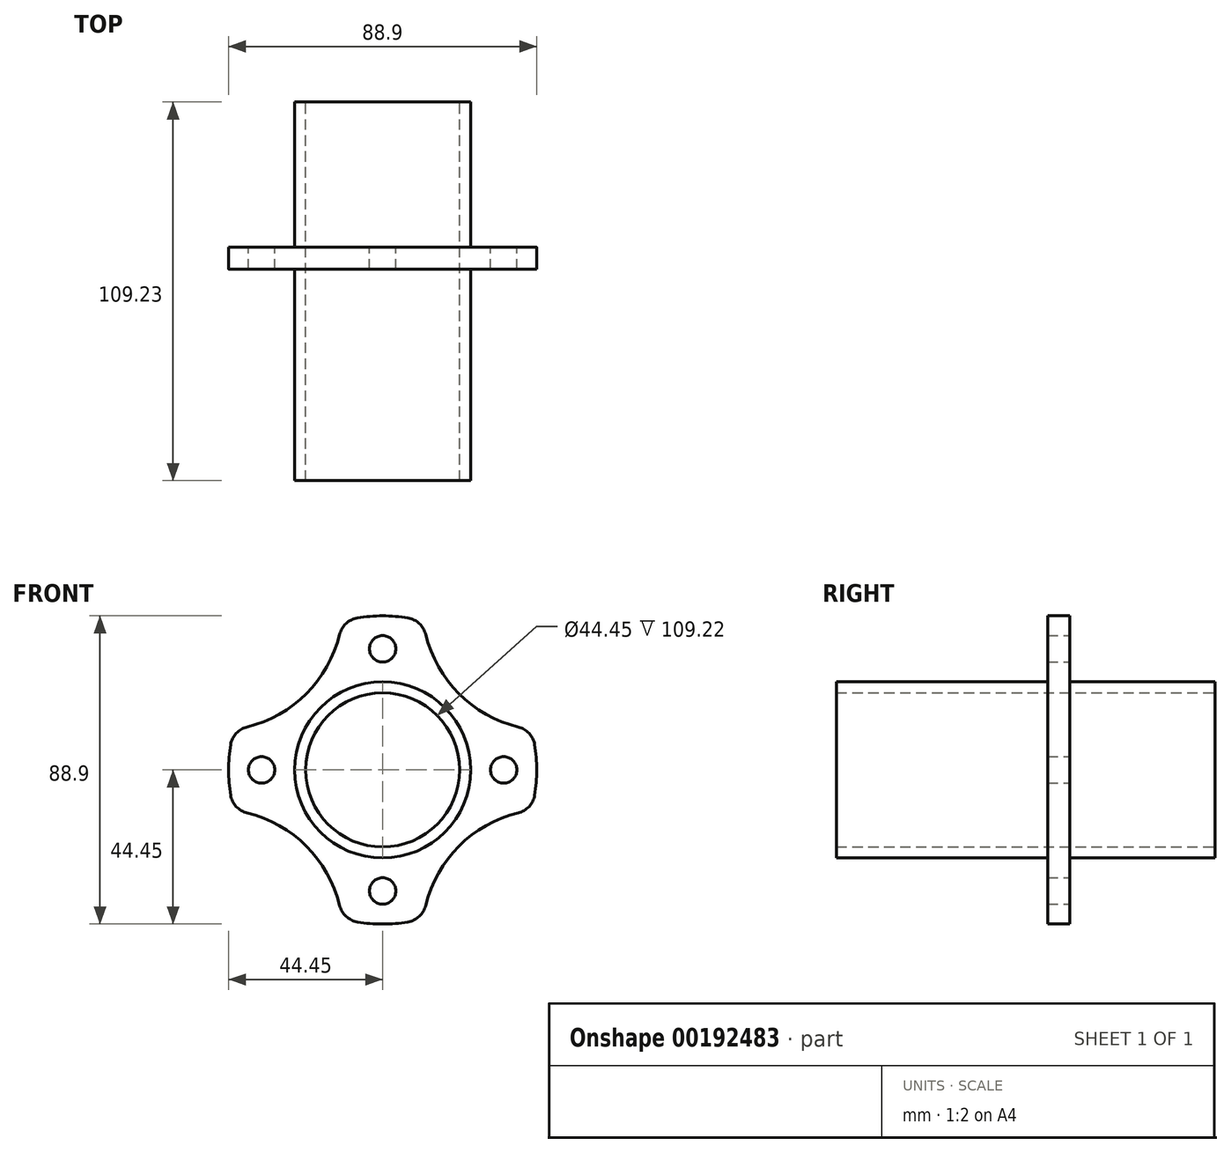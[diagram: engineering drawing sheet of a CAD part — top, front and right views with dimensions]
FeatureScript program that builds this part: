
annotation { "Feature Type Name" : "Feature", "Feature Type Description" : "" }
export const myFeature = defineFeature(function(context is Context, id is Id, definition is map)
    precondition{}
    {
        {
            var Q0;
            Q0=qCreatedBy(makeId("Front.planeOp"),FACE);
            cPlane(context, id + "F0", {"entities" : qUnion([Q0]), "cplaneType" : CPlaneType.OFFSET, "offset" : 9.52 * mm, "width" : 152.4 * mm, "height" : 152.4 * mm});
        }
        {
            var Q0;
            Q0=qCreatedBy(id+"F0.planeOp",FACE);
            var sketch = newSketch(context, id + "F1", { "sketchPlane" : qUnion([Q0])});
            skCircle(sketch, "E0", {"center": v(0, 0) * mm, "radius": 25.4 * mm});
            skCircle(sketch, "E1", {"center": v(0, 0) * mm, "radius": 22.23 * mm});
            skSolve(sketch);
        }
        {
            var Q0;
            Q0 = qSketchRegion(id + "F1", true);
            extrude(context, id + "F2", {"entities" : qUnion([Q0]), "endBound" : BoundingType.SYMMETRIC, "depth" : 109.22 * mm});
        }
        {
            var Q0;
            Q0=qCreatedBy(makeId("Front.planeOp"),FACE);
            var sketch = newSketch(context, id + "F3", { "sketchPlane" : qUnion([Q0])});
            skCircle(sketch, "E2", {"center": v(0, 0) * mm, "radius": 25.4 * mm});
            skCircle(sketch, "E3", {"center": v(0, 0) * mm, "radius": 44.45 * mm});
            skCircle(sketch, "E4", {"center": v(0, 0) * mm, "radius": 34.93 * mm, "construction": true});
            skCircle(sketch, "E5", {"center": v(0, 34.93) * mm, "radius": 3.81 * mm});
            skCircle(sketch, "E6.1.0", {"center": v(-34.93, 0) * mm, "radius": 3.81 * mm});
            skCircle(sketch, "E6.2.0", {"center": v(0, -34.93) * mm, "radius": 3.81 * mm});
            skCircle(sketch, "E6.3.0", {"center": v(34.93, 0) * mm, "radius": 3.81 * mm});
            skLineSegment(sketch, "E7.bottom", {"start": v(-47.62, 47.63) * mm, "end": v(47.63, 47.63) * mm, "construction": true});
            skLineSegment(sketch, "E7.top", {"start": v(-47.63, -47.63) * mm, "end": v(47.62, -47.63) * mm, "construction": true});
            skLineSegment(sketch, "E7.left", {"start": v(-47.62, 47.63) * mm, "end": v(-47.63, -47.63) * mm, "construction": true});
            skLineSegment(sketch, "E7.right", {"start": v(47.63, 47.63) * mm, "end": v(47.63, -47.63) * mm, "construction": true});
            skCircle(sketch, "E8", {"center": v(0, 0) * mm, "radius": 31.12 * mm, "construction": true});
            skArc(sketch, "E9", {"start": v(-42.88, 11.7) * mm, "mid": v(-22, 22) * mm, "end": v(-11.7, 42.88) * mm});
            skArc(sketch, "E10", {"start": v(-11.7, -42.88) * mm, "mid": v(-22, -22) * mm, "end": v(-42.88, -11.7) * mm});
            skArc(sketch, "E11", {"start": v(42.88, -11.7) * mm, "mid": v(22, -22) * mm, "end": v(11.7, -42.88) * mm});
            skArc(sketch, "E12", {"start": v(11.7, 42.88) * mm, "mid": v(22, 22) * mm, "end": v(42.88, 11.7) * mm});
            skPoint(sketch, "E13.center.orphan", {"position": v(-47.63, 0) * mm});
            skPoint(sketch, "E14.center.orphan", {"position": v(0, 47.63) * mm});
            skPoint(sketch, "E15.center.orphan", {"position": v(0, -47.63) * mm});
            skPoint(sketch, "E16.center.orphan", {"position": v(47.63, 0) * mm});
            skSolve(sketch);
        }
        {
            var Q0;
            Q0=makeQuery(id+"F3.imprint","IMPRINT",FACE,{"disambiguationData":[TD([[makeQuery(id+"F3.imprint","IMPRINT",EDGE,{"derivedFrom":sQuery(id+"F3.wireOp",EDGE,"E2")}),-1.0]])]});
            extrude(context, id + "F4", {"entities" : qUnion([Q0]), "operationType" : NewBodyOperationType.ADD, "endBound" : BoundingType.SYMMETRIC, "depth" : 6.35 * mm});
        }
        {
            var Q0;
            {var subQ0=sQuery(id+"F3.wireOp",EDGE,"E12");var subQ1=sQuery(id+"F3.wireOp",EDGE,"E3");Q0=makeQuery(id+"F4.opExtrude","SWEPT_EDGE",EDGE,{"disambiguationData":[OSD([subQ1,subQ0]),TDD([makeQuery(id+"F3.imprint","INTERSECT",VERTEX,{"disambiguationData":[OD(0.0)],"derivedFrom":[subQ1,subQ0]})])]});}
            var Q1;
            {var subQ0=sQuery(id+"F3.wireOp",EDGE,"E12");var subQ1=sQuery(id+"F3.wireOp",EDGE,"E3");Q1=makeQuery(id+"F4.opExtrude","SWEPT_EDGE",EDGE,{"disambiguationData":[OSD([subQ1,subQ0]),TDD([makeQuery(id+"F3.imprint","INTERSECT",VERTEX,{"disambiguationData":[OD(1.0)],"derivedFrom":[subQ1,subQ0]})])]});}
            var Q2;
            {var subQ0=sQuery(id+"F3.wireOp",EDGE,"E9");var subQ1=sQuery(id+"F3.wireOp",EDGE,"E3");Q2=makeQuery(id+"F4.opExtrude","SWEPT_EDGE",EDGE,{"disambiguationData":[OSD([subQ1,subQ0]),TDD([makeQuery(id+"F3.imprint","INTERSECT",VERTEX,{"disambiguationData":[OD(1.0)],"derivedFrom":[subQ1,subQ0]})])]});}
            var Q3;
            {var subQ0=sQuery(id+"F3.wireOp",EDGE,"E9");var subQ1=sQuery(id+"F3.wireOp",EDGE,"E3");Q3=makeQuery(id+"F4.opExtrude","SWEPT_EDGE",EDGE,{"disambiguationData":[OSD([subQ1,subQ0]),TDD([makeQuery(id+"F3.imprint","INTERSECT",VERTEX,{"disambiguationData":[OD(0.0)],"derivedFrom":[subQ1,subQ0]})])]});}
            var Q4;
            {var subQ0=sQuery(id+"F3.wireOp",EDGE,"E10");var subQ1=sQuery(id+"F3.wireOp",EDGE,"E3");Q4=makeQuery(id+"F4.opExtrude","SWEPT_EDGE",EDGE,{"disambiguationData":[OSD([subQ1,subQ0]),TDD([makeQuery(id+"F3.imprint","INTERSECT",VERTEX,{"disambiguationData":[OD(1.0)],"derivedFrom":[subQ1,subQ0]})])]});}
            var Q5;
            {var subQ0=sQuery(id+"F3.wireOp",EDGE,"E10");var subQ1=sQuery(id+"F3.wireOp",EDGE,"E3");Q5=makeQuery(id+"F4.opExtrude","SWEPT_EDGE",EDGE,{"disambiguationData":[OSD([subQ1,subQ0]),TDD([makeQuery(id+"F3.imprint","INTERSECT",VERTEX,{"disambiguationData":[OD(0.0)],"derivedFrom":[subQ1,subQ0]})])]});}
            var Q6;
            {var subQ0=sQuery(id+"F3.wireOp",EDGE,"E11");var subQ1=sQuery(id+"F3.wireOp",EDGE,"E3");Q6=makeQuery(id+"F4.opExtrude","SWEPT_EDGE",EDGE,{"disambiguationData":[OSD([subQ1,subQ0]),TDD([makeQuery(id+"F3.imprint","INTERSECT",VERTEX,{"disambiguationData":[OD(1.0)],"derivedFrom":[subQ1,subQ0]})])]});}
            var Q7;
            {var subQ0=sQuery(id+"F3.wireOp",EDGE,"E11");var subQ1=sQuery(id+"F3.wireOp",EDGE,"E3");Q7=makeQuery(id+"F4.opExtrude","SWEPT_EDGE",EDGE,{"disambiguationData":[OSD([subQ1,subQ0]),TDD([makeQuery(id+"F3.imprint","INTERSECT",VERTEX,{"disambiguationData":[OD(0.0)],"derivedFrom":[subQ1,subQ0]})])]});}
            fillet(context, id + "F5", {"entities" : qUnion([Q0, Q1, Q2, Q3, Q4, Q5, Q6, Q7]), "radius" : 6.35 * mm, "tangentPropagation" : true, "allowEdgeOverflow" : false});
        }
    });
